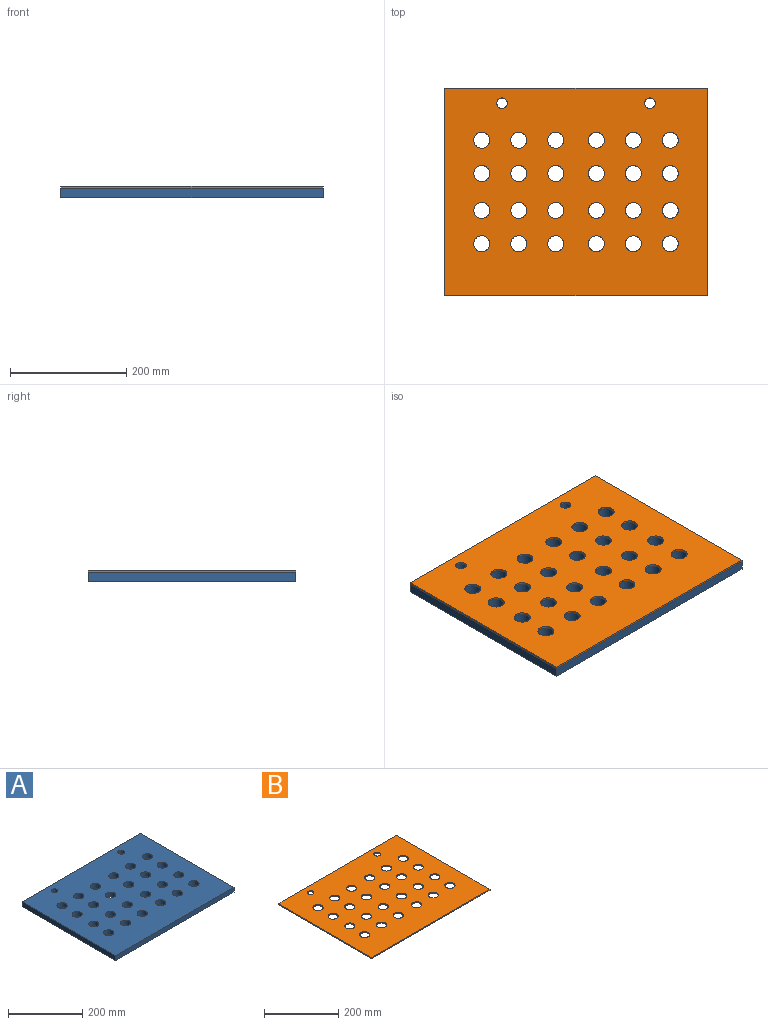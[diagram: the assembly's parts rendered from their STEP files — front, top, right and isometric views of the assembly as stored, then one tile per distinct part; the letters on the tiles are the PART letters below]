
ASSEMBLY  parts=2 mates=1
PART A: 32 faces, bbox 450.9x355.6x15.9 mm
  f0: plane 450.85x15.88mm, normal (0,1,0), area 7157.2mm2, adj f1,f3,f4,f5
  f1: plane 355.6x15.88mm, normal (-1,0,0), area 5645.2mm2, adj f0,f2,f4,f5
  f2: plane 450.85x15.88mm, normal (0,-1,0), area 7157.2mm2, adj f1,f3,f4,f5
  f3: plane 355.6x15.88mm, normal (1,0,0), area 5645.2mm2, adj f0,f2,f4,f5
  f4: plane 450.85x355.6mm, normal (0,0,1), area 145698.3mm2, adj f0,f1,f2,f3,f6,f7,f8,f9
  f5: plane 450.85x355.6mm, normal (0,0,-1), area 145698.3mm2, adj f0,f1,f2,f3,f6,f7,f8,f9
  f6: cylinder r=13.68mm len=27.36mm, axis (0,0,1), area 1364.3mm2, adj f4,f5
  f7: cylinder r=13.68mm len=27.36mm, axis (0,0,1), area 1364.3mm2, adj f4,f5
  f8: cylinder r=13.68mm len=27.36mm, axis (0,0,1), area 1364.3mm2, adj f4,f5
  f9: cylinder r=13.68mm len=27.36mm, axis (0,0,1), area 1364.3mm2, adj f4,f5
  f10: cylinder r=13.68mm len=27.36mm, axis (0,0,1), area 1364.3mm2, adj f4,f5
  f11: cylinder r=13.68mm len=27.36mm, axis (0,0,1), area 1364.3mm2, adj f4,f5
  f12: cylinder r=13.68mm len=27.36mm, axis (0,0,1), area 1364.3mm2, adj f4,f5
  f13: cylinder r=13.68mm len=27.36mm, axis (0,0,1), area 1364.3mm2, adj f4,f5
  f14: cylinder r=13.68mm len=27.36mm, axis (0,0,1), area 1364.3mm2, adj f4,f5
  f15: cylinder r=13.68mm len=27.36mm, axis (0,0,1), area 1364.3mm2, adj f4,f5
  f16: cylinder r=13.68mm len=27.36mm, axis (0,0,1), area 1364.3mm2, adj f4,f5
  f17: cylinder r=13.68mm len=27.36mm, axis (0,0,1), area 1364.3mm2, adj f4,f5
  f18: cylinder r=13.68mm len=27.36mm, axis (0,0,1), area 1364.3mm2, adj f4,f5
  f19: cylinder r=13.68mm len=27.36mm, axis (0,0,1), area 1364.3mm2, adj f4,f5
  f20: cylinder r=13.68mm len=27.36mm, axis (0,0,1), area 1364.3mm2, adj f4,f5
  f21: cylinder r=13.68mm len=27.36mm, axis (0,0,1), area 1364.3mm2, adj f4,f5
  f22: cylinder r=13.68mm len=27.36mm, axis (0,0,1), area 1364.3mm2, adj f4,f5
  f23: cylinder r=13.68mm len=27.36mm, axis (0,0,1), area 1364.3mm2, adj f4,f5
  f24: cylinder r=13.68mm len=27.36mm, axis (0,0,1), area 1364.3mm2, adj f4,f5
  f25: cylinder r=13.68mm len=27.36mm, axis (0,0,1), area 1364.3mm2, adj f4,f5
  f26: cylinder r=13.68mm len=27.36mm, axis (0,0,1), area 1364.3mm2, adj f4,f5
  f27: cylinder r=13.68mm len=27.36mm, axis (0,0,1), area 1364.3mm2, adj f4,f5
  f28: cylinder r=13.68mm len=27.36mm, axis (0,0,1), area 1364.3mm2, adj f4,f5
  f29: cylinder r=13.68mm len=27.36mm, axis (0,0,1), area 1364.3mm2, adj f4,f5
  f30: cylinder r=9.08mm len=18.16mm, axis (0,0,1), area 905.7mm2, adj f4,f5
  f31: cylinder r=9.08mm len=18.16mm, axis (0,0,1), area 905.7mm2, adj f4,f5
PART B: 32 faces, bbox 450.9x355.6x3.2 mm
  f0: plane 450.85x3.18mm, normal (0,1,0), area 1431.4mm2, adj f1,f3,f4,f5
  f1: plane 355.6x3.18mm, normal (-1,0,0), area 1129mm2, adj f0,f2,f4,f5
  f2: plane 450.85x3.18mm, normal (0,-1,0), area 1431.4mm2, adj f1,f3,f4,f5
  f3: plane 355.6x3.18mm, normal (1,0,0), area 1129mm2, adj f0,f2,f4,f5
  f4: plane 450.85x355.6mm, normal (0,0,1), area 145698.3mm2, adj f0,f1,f2,f3,f6,f7,f8,f9
  f5: plane 450.85x355.6mm, normal (0,0,-1), area 145698.3mm2, adj f0,f1,f2,f3,f6,f7,f8,f9
  f6: cylinder r=13.68mm len=27.36mm, axis (0,0,1), area 272.9mm2, adj f4,f5
  f7: cylinder r=13.68mm len=27.36mm, axis (0,0,1), area 272.9mm2, adj f4,f5
  f8: cylinder r=13.68mm len=27.36mm, axis (0,0,1), area 272.9mm2, adj f4,f5
  f9: cylinder r=13.68mm len=27.36mm, axis (0,0,1), area 272.9mm2, adj f4,f5
  f10: cylinder r=13.68mm len=27.36mm, axis (0,0,1), area 272.9mm2, adj f4,f5
  f11: cylinder r=13.68mm len=27.36mm, axis (0,0,1), area 272.9mm2, adj f4,f5
  f12: cylinder r=13.68mm len=27.36mm, axis (0,0,1), area 272.9mm2, adj f4,f5
  f13: cylinder r=13.68mm len=27.36mm, axis (0,0,1), area 272.9mm2, adj f4,f5
  f14: cylinder r=13.68mm len=27.36mm, axis (0,0,1), area 272.9mm2, adj f4,f5
  f15: cylinder r=13.68mm len=27.36mm, axis (0,0,1), area 272.9mm2, adj f4,f5
  f16: cylinder r=13.68mm len=27.36mm, axis (0,0,1), area 272.9mm2, adj f4,f5
  f17: cylinder r=13.68mm len=27.36mm, axis (0,0,1), area 272.9mm2, adj f4,f5
  f18: cylinder r=13.68mm len=27.36mm, axis (0,0,1), area 272.9mm2, adj f4,f5
  f19: cylinder r=13.68mm len=27.36mm, axis (0,0,1), area 272.9mm2, adj f4,f5
  f20: cylinder r=13.68mm len=27.36mm, axis (0,0,1), area 272.9mm2, adj f4,f5
  f21: cylinder r=13.68mm len=27.36mm, axis (0,0,1), area 272.9mm2, adj f4,f5
  f22: cylinder r=13.68mm len=27.36mm, axis (0,0,1), area 272.9mm2, adj f4,f5
  f23: cylinder r=13.68mm len=27.36mm, axis (0,0,1), area 272.9mm2, adj f4,f5
  f24: cylinder r=13.68mm len=27.36mm, axis (0,0,1), area 272.9mm2, adj f4,f5
  f25: cylinder r=13.68mm len=27.36mm, axis (0,0,1), area 272.9mm2, adj f4,f5
  f26: cylinder r=13.68mm len=27.36mm, axis (0,0,1), area 272.9mm2, adj f4,f5
  f27: cylinder r=13.68mm len=27.36mm, axis (0,0,1), area 272.9mm2, adj f4,f5
  f28: cylinder r=13.68mm len=27.36mm, axis (0,0,1), area 272.9mm2, adj f4,f5
  f29: cylinder r=13.68mm len=27.36mm, axis (0,0,1), area 272.9mm2, adj f4,f5
  f30: cylinder r=9.08mm len=18.16mm, axis (0,0,1), area 181.1mm2, adj f4,f5
  f31: cylinder r=9.08mm len=18.16mm, axis (0,0,1), area 181.1mm2, adj f4,f5
PLACE A t=(1.78,0.27,-9.07)mm fixed
PLACE B t=(1.78,0.27,-9.07)mm
MATE fastened A.f4 <-> B.f5  axis (0,0,1) through (1.78,-0.27,6.8)mm
